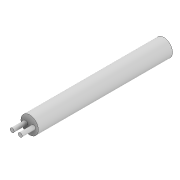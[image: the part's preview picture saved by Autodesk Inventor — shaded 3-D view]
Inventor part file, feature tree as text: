
AUTODESK INVENTOR PART (.ipt)
format: ipt  version: 2020 (Build 240168000, 168)  size: 83,968 bytes
history: native  units: mm
features: extrude x2, sketch x2
ambient origin geometry x8: Origin, YZ Plane, XZ Plane, XY Plane, X Axis, Y Axis, Z Axis, Center Point
bodies: Volumenkörper1 (feature_tree)
feature tree (4):
  extrude  "Extrusion1"  Depth=50.0mm TaperAngle=0.0deg
  extrude  "Extrusion2"  Depth=5.0mm
  sketch  "Skizze1"  dims[d0=6.5mm d1=50.0mm d2=0.0mm]
  sketch  "Skizze2"  dims[d3=1.5mm d4=1.5mm d5=1.5mm d6=1.5mm d7=5.0mm d8=0.0mm]
